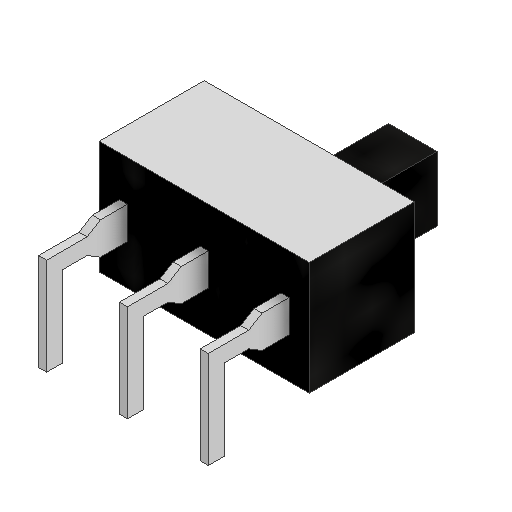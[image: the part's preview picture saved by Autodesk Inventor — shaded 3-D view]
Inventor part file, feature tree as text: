
AUTODESK INVENTOR PART (.ipt)
format: ipt  version: 2025.2 (Build 292293000, 293)  size: 177,152 bytes
history: native  units: mm
features: extrude x4, sketch x4, pattern_linear x1, mirror x1
ambient origin geometry x8: Origin, YZ Plane, XZ Plane, XY Plane, X Axis, Y Axis, Z Axis, Center Point
bodies: Solid1 (feature_tree)
feature tree (10):
  extrude  "Extrusion1"  Depth=7.0mm
  extrude  "Extrusion2"  Depth=4.0mm
  extrude  "Extrusion3"  Depth=0.1mm TaperAngle=0.0deg
  extrude  "Extrusion4"  Depth=1.0mm
  pattern_linear  "Rectangular Pattern1"  Spacing1=1.0mm  [1 undecoded]
  mirror  "Mirror1"
  sketch  "Sketch1"  dims[d0=13.0mm d1=7.0mm]
  sketch  "Sketch2"  dims[d2=6.5mm d3=0.0mm d4=4.0mm]
  sketch  "Sketch3"  dims[d5=6.0mm d6=0.1mm d7=0.0mm]
  sketch  "Sketch4"  dims[d8=5.0mm d9=0.0mm d10=1.0mm d11=1.0mm d12=2.0mm d13=2.0mm d14=5.0mm d15=0.5mm d16=0.0mm d17=20.0mm d19=5.0mm]
note: 1 required parameter value undecoded (feature->parameter linkage not recoverable at this tier; creation-order binding heuristic only, values carry confidence <= 0.55)
